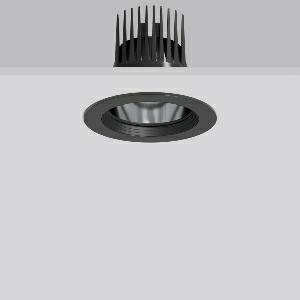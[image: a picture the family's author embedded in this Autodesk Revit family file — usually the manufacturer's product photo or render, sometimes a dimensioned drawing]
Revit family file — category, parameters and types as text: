
# Revit family: heledon_maxi_e_901766_003_1_31ea
name_source: partatom
category: Lighting Fixtures
units: mm (PartAtom-declared; Revit-internal decimal feet)

## family parameters
Cut with Voids When Loaded = No
Host = Face
Light Source = No
Part Type = Normal
Room Calculation Point = No
Round Connector Dimension = Use Diameter
Shared = No

## types (1)
- HELEDON maxi E (1 x LED Modul 940, 4400 lm, 4000)
    Apparent Load = 35 VA
    Approval mark = CE
    CIE Flux Codes = 97 100 100 100 100
    Color Rendering = 92
    Color Temperature = 4000
    Default Elevation = 1800 mm
    Description = Series: HELEDON maxi
Round recessed downlight. Housing: die-cast aluminium, powder-coated. Black plastic ring and recessed LED to prevent glare from the side. Optical assembly with reflector made of MIRO-Silver with 98% total light reflection for outstanding efficiency - can be changed without tools. Best colour rendering index Ra>90. Suitable for Recessed ceiling mounting. Installation without tools thanks to spring fastening system. Including separate LED converter with connecting cable 600 mm.High quality converter without flickering and stroboscopic effect. Through-wiring box (5 pole) available as accessory. The following accessories can be mounted without use of tools: interchangeable lenses, decorative glasses, honeycomb louvre, clear and frosted diffusers, white interchangeable plastic ring. 
Colour: deep black, matt (RAL 9005)
Diameter: 162 mm
Height: 3 mm
Cut-out diameter: 152 mm
Recess height: 200 mm
Luminaire: recess height: 135 mm
Lamp: LED
Socket: without socket
Colour temperature: 4000K
Colour rendering index (CRI): 92
System power: 35 W
Rated luminous flux: 4400 lm
Luminous efficiency: 126 lm/W
Control gear: Regulated power supply
Protection class: II
Type of protection: IP 20
    Height = 0 mm  [stored 0 ft]
    Lamp = 1 x LED Modul 940
    Lamp Light Flux = 4400 lm
    Lamp count = 1
    Length = 162 mm
    Lifetime = 50000 h
    Luminous efficacy = 126 lm/W
    Manufacturer = RZB
    ModVariant = No
    Model = 901766.003.1
    Mounting Place = Ceiling
    Mounting Type = Recessed
    Number of Poles = 1
    OnlyDefault = Yes
    Power Factor = 1
    Product Name = HELEDON maxi E
    Product group = Recessed downlights
    ProductGroupID = 402
    Protection Class = Protection class II
    Protection Degree = IP 20
    RLX_Detail_Level = 1
    RLX_Emergency_Light_Flux = 0 lm
    RLX_Emergency_Type = 0
    RLX_Emergency_Type_DB = No
    RlxData = <blob elided: 124285 chars, md5=8d9d32eb>
    Socket = socket
    Standby Power = 0 W
    System Light Flux = 4400 lm
    System Power = 35 W
    Type Comments = Product without accessories
    Type Image = 901662.003.jpg
    URL = http://relux.com
    VarID = ---
    Voltage = 230 V
    Voltage Range = 220-240 V
    Weight = 0.00 kg
    Width = 0 mm  [stored 0 ft]

note: [stored X ft] marks values corroborated as IEEE doubles in the binary element streams (Revit-internal decimal feet)

## geometry (parser evidence)
native form markers: Blend x4, Sweep x12
no freeform markers — native parametric forms only
